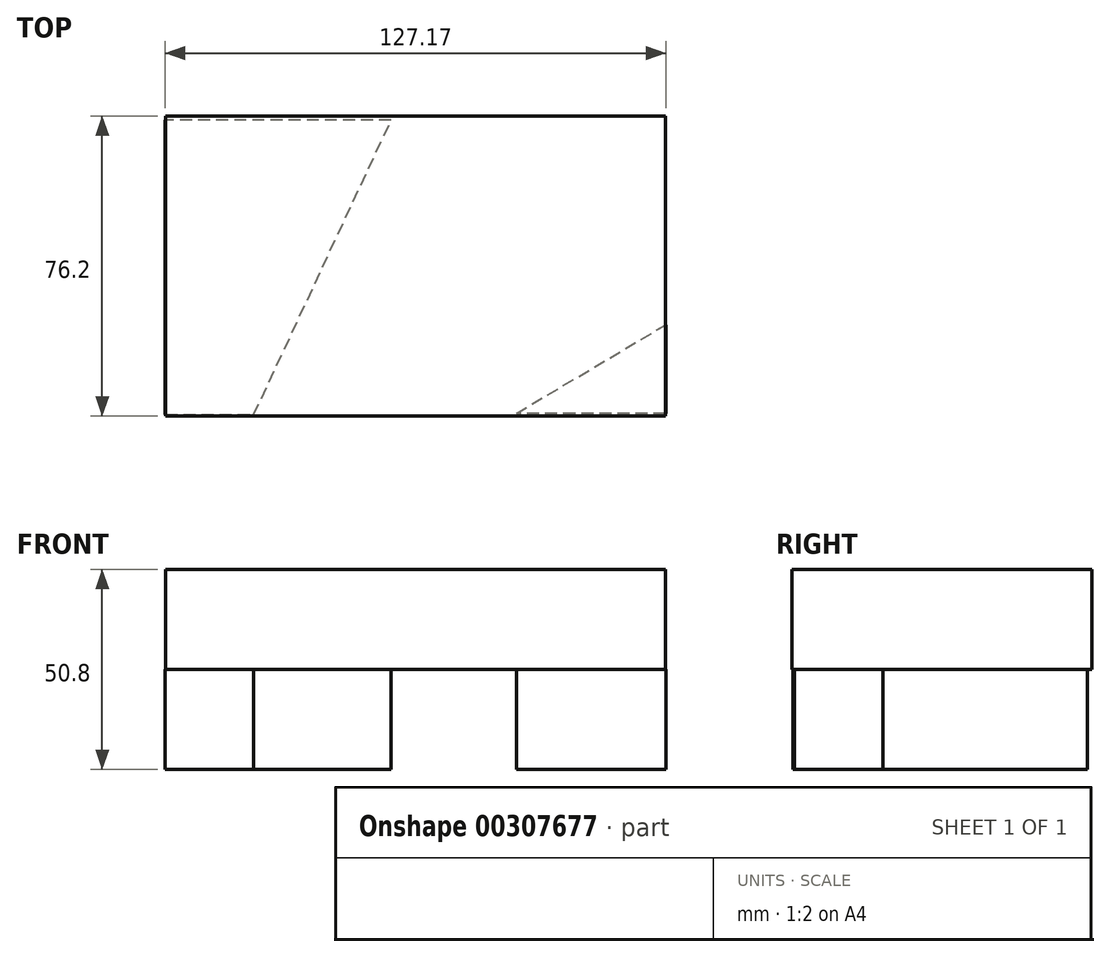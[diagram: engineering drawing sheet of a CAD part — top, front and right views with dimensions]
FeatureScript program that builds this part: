
annotation { "Feature Type Name" : "Feature", "Feature Type Description" : "" }
export const myFeature = defineFeature(function(context is Context, id is Id, definition is map)
    precondition{}
    {
        {
            var Q0;
            Q0=qCreatedBy(makeId("Top.planeOp"),FACE);
            var sketch = newSketch(context, id + "F0", { "sketchPlane" : qUnion([Q0])});
            skLineSegment(sketch, "E0", {"start": v(-57.28, -36.58) * mm, "end": v(-57.28, 39.62) * mm});
            skLineSegment(sketch, "E1", {"start": v(-57.28, 39.62) * mm, "end": v(69.72, 39.62) * mm});
            skLineSegment(sketch, "E2", {"start": v(69.72, 39.62) * mm, "end": v(69.72, -36.58) * mm});
            skLineSegment(sketch, "E3", {"start": v(69.72, -36.58) * mm, "end": v(-57.28, -36.58) * mm});
            skSolve(sketch);
        }
        {
            var Q0;
            Q0=makeQuery(id+"F0.imprint","IMPRINT",FACE,{"disambiguationData":[TD([[makeQuery(id+"F0.imprint","IMPRINT",EDGE,{"derivedFrom":sQuery(id+"F0.wireOp",EDGE,"E0")}),-1.0]])]});
            extrude(context, id + "F1", {"entities" : qUnion([Q0]), "depth" : 25.4 * mm});
        }
        {
            var Q0;
            Q0=qCreatedBy(makeId("Top.planeOp"),FACE);
            var sketch = newSketch(context, id + "F2", { "sketchPlane" : qUnion([Q0])});
            skLineSegment(sketch, "E4", {"start": v(-57.37, -36.26) * mm, "end": v(-34.88, -36.26) * mm});
            skLineSegment(sketch, "E5", {"start": v(-34.88, -36.26) * mm, "end": v(0, 38.56) * mm});
            skLineSegment(sketch, "E6", {"start": v(0, 38.56) * mm, "end": v(-57.37, 38.56) * mm});
            skLineSegment(sketch, "E7", {"start": v(-57.37, 38.56) * mm, "end": v(-57.37, -36.26) * mm});
            skLineSegment(sketch, "E8", {"start": v(69.8, -35.91) * mm, "end": v(31.86, -35.91) * mm});
            skLineSegment(sketch, "E9", {"start": v(31.86, -35.91) * mm, "end": v(69.8, -13.43) * mm});
            skLineSegment(sketch, "E10", {"start": v(69.8, -13.43) * mm, "end": v(69.8, -35.91) * mm});
            skSolve(sketch);
        }
        {
            var Q0;
            Q0=makeQuery(id+"F2.imprint","IMPRINT",FACE,{"disambiguationData":[TD([[makeQuery(id+"F2.imprint","IMPRINT",EDGE,{"derivedFrom":sQuery(id+"F2.wireOp",EDGE,"E4")}),1.0]])]});
            var Q1;
            Q1=makeQuery(id+"F2.imprint","IMPRINT",FACE,{"disambiguationData":[TD([[makeQuery(id+"F2.imprint","IMPRINT",EDGE,{"derivedFrom":sQuery(id+"F2.wireOp",EDGE,"E8")}),-1.0]])]});
            extrude(context, id + "F3", {"entities" : qUnion([Q0, Q1]), "oppositeDirection" : true, "depth" : 25.4 * mm});
        }
    });
